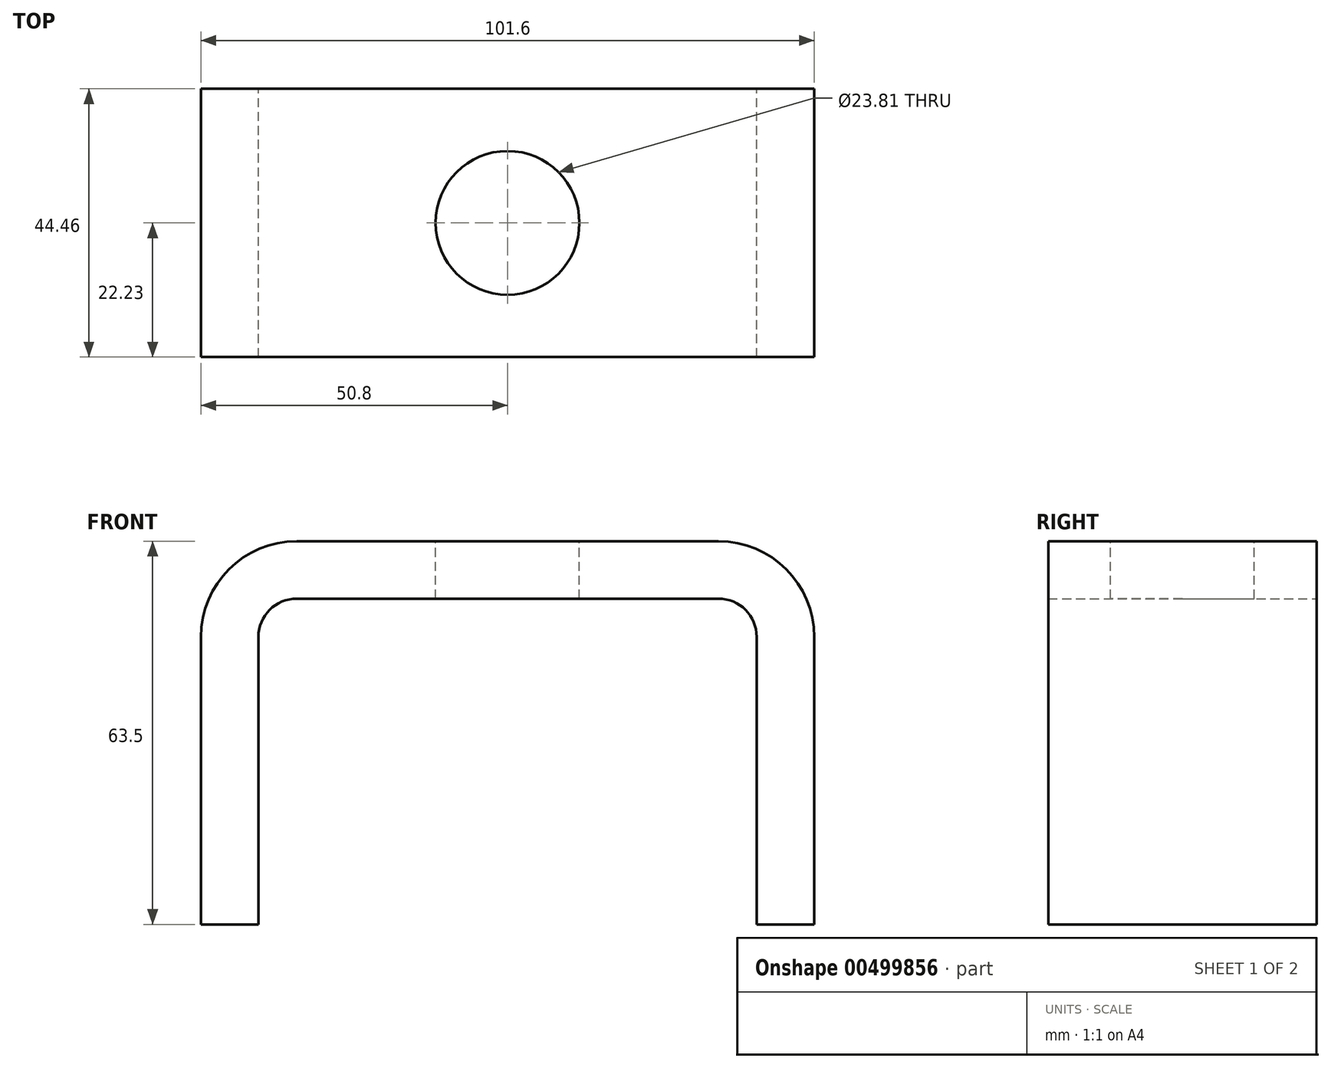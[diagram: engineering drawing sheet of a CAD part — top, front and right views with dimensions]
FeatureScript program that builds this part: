
annotation { "Feature Type Name" : "Feature", "Feature Type Description" : "" }
export const myFeature = defineFeature(function(context is Context, id is Id, definition is map)
    precondition{}
    {
        {
            var Q0;
            Q0=qCreatedBy(makeId("Front.planeOp"),FACE);
            var sketch = newSketch(context, id + "F0", { "sketchPlane" : qUnion([Q0])});
            skLineSegment(sketch, "E0.top", {"start": v(41.28, 41.28) * mm, "end": v(-41.28, 41.27) * mm});
            skLineSegment(sketch, "E0.left", {"start": v(41.28, -41.27) * mm, "end": v(41.28, 41.28) * mm});
            skLineSegment(sketch, "E0.right", {"start": v(-41.28, -41.28) * mm, "end": v(-41.28, 41.28) * mm});
            skPoint(sketch, "E0.middle", {"position": v(0, 0) * mm});
            skLineSegment(sketch, "E1.0", {"start": v(41.27, 50.8) * mm, "end": v(-41.28, 50.8) * mm});
            skLineSegment(sketch, "E2.0", {"start": v(-50.8, -12.7) * mm, "end": v(-50.8, 50.8) * mm});
            skLineSegment(sketch, "E2.1", {"start": v(50.8, -12.7) * mm, "end": v(41.28, -12.7) * mm});
            skLineSegment(sketch, "E2.2", {"start": v(50.8, -12.7) * mm, "end": v(50.8, 50.8) * mm});
            skLineSegment(sketch, "E2.3", {"start": v(50.8, 50.8) * mm, "end": v(-50.8, 50.8) * mm});
            skLineSegment(sketch, "E3", {"start": v(-41.28, -12.7) * mm, "end": v(-41.28, -41.28) * mm});
            skLineSegment(sketch, "E4", {"start": v(41.28, -12.7) * mm, "end": v(41.28, -41.27) * mm});
            skLineSegment(sketch, "E5.trimOffspring", {"start": v(-41.28, -12.7) * mm, "end": v(-50.8, -12.7) * mm});
            skSolve(sketch);
        }
        {
            var Q0;
            Q0 = qSketchRegion(id + "F0", true);
            extrude(context, id + "F1", {"entities" : qUnion([Q0]), "endBound" : BoundingType.SYMMETRIC, "depth" : 44.45 * mm});
        }
        {
            var Q0;
            Q0=makeQuery(id+"F1.opExtrude","SWEPT_EDGE",EDGE,{"disambiguationData":[OSD([sQuery(id+"F0.wireOp",EDGE,"E0.top"),sQuery(id+"F0.wireOp",EDGE,"E0.right")])]});
            var Q1;
            Q1=makeQuery(id+"F1.opExtrude","SWEPT_EDGE",EDGE,{"disambiguationData":[OSD([sQuery(id+"F0.wireOp",EDGE,"E0.top"),sQuery(id+"F0.wireOp",EDGE,"E0.left")])]});
            fillet(context, id + "F2", {"entities" : qUnion([Q0, Q1]), "radius" : 6.35 * mm, "tangentPropagation" : true, "allowEdgeOverflow" : false});
        }
        {
            var Q0;
            Q0=makeQuery(id+"F1.opExtrude","SWEPT_EDGE",EDGE,{"disambiguationData":[OSD([sQuery(id+"F0.wireOp",EDGE,"E2.2"),sQuery(id+"F0.wireOp",EDGE,"E2.3")])]});
            var Q1;
            Q1=makeQuery(id+"F1.opExtrude","SWEPT_EDGE",EDGE,{"disambiguationData":[OSD([sQuery(id+"F0.wireOp",EDGE,"E2.0"),sQuery(id+"F0.wireOp",EDGE,"E2.3")])]});
            fillet(context, id + "F3", {"entities" : qUnion([Q0, Q1]), "radius" : 15.88 * mm, "tangentPropagation" : true, "allowEdgeOverflow" : false});
        }
        {
            var Q0;
            Q0=makeQuery(id+"F1.opExtrude","SWEPT_FACE",FACE,{"disambiguationData":[OSD([sQuery(id+"F0.wireOp",EDGE,"E2.3")])]});
            var sketch = newSketch(context, id + "F4", { "sketchPlane" : qUnion([Q0])});
            skCircle(sketch, "E6", {"center": v(0, 0) * mm, "radius": 11.9 * mm});
            skSolve(sketch);
        }
        {
            var Q0;
            Q0 = qSketchRegion(id + "F4", true);
            extrude(context, id + "F5", {"entities" : qUnion([Q0]), "operationType" : NewBodyOperationType.REMOVE, "oppositeDirection" : true, "depth" : 25.4 * mm});
        }
    });
